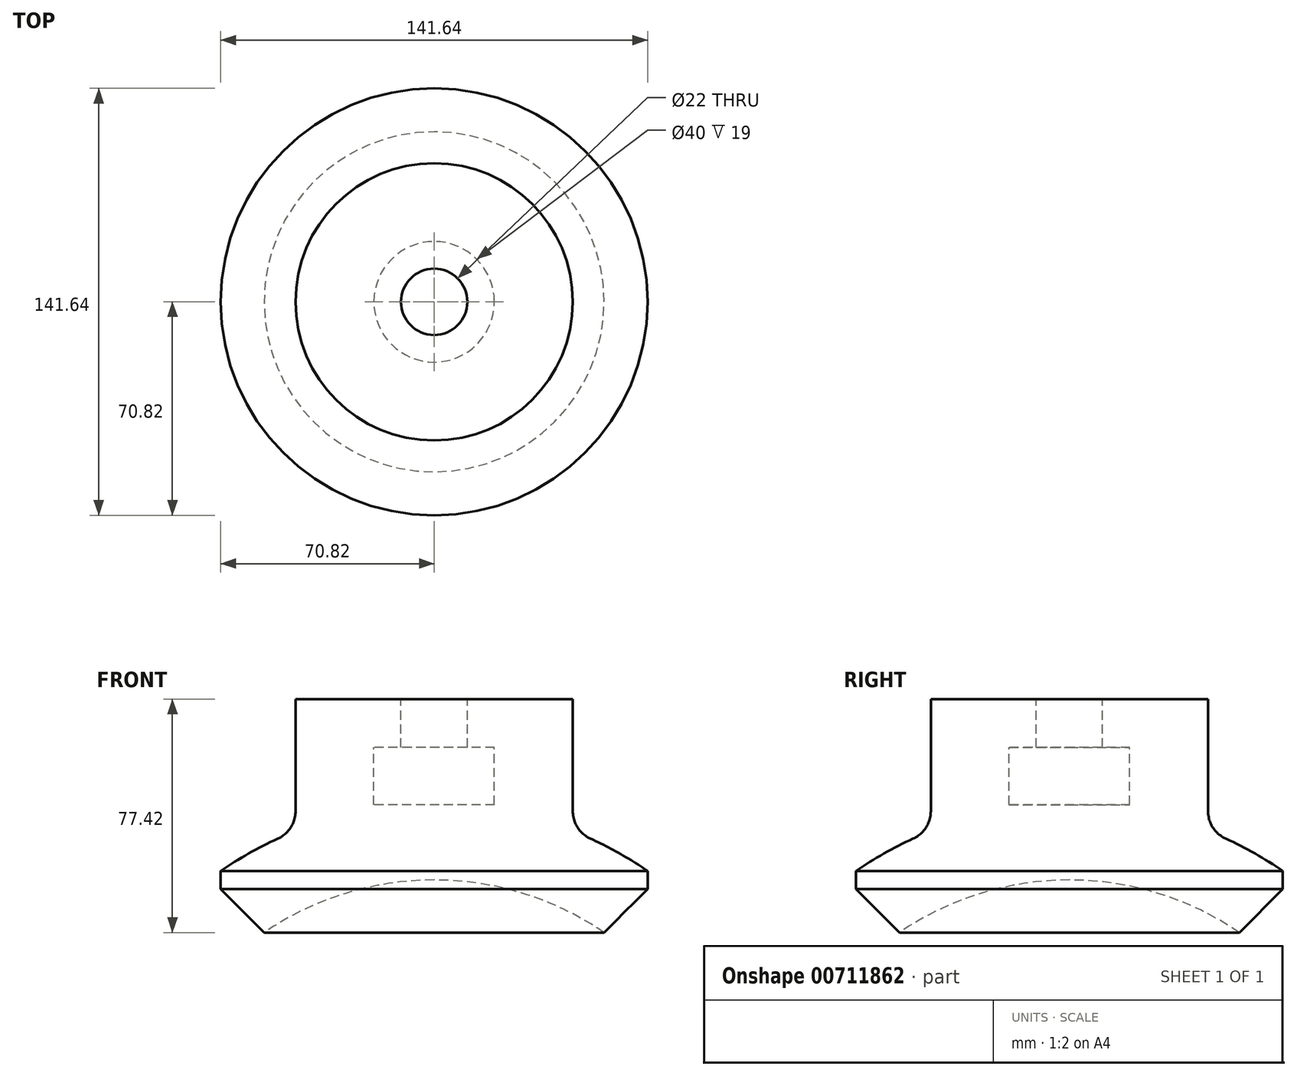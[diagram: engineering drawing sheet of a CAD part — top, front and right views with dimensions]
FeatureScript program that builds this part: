
annotation { "Feature Type Name" : "Feature", "Feature Type Description" : "" }
export const myFeature = defineFeature(function(context is Context, id is Id, definition is map)
    precondition{}
    {
        {
            var Q0;
            Q0=qCreatedBy(makeId("Front.planeOp"),FACE);
            var sketch = newSketch(context, id + "F0", { "sketchPlane" : qUnion([Q0])});
            skLineSegment(sketch, "E0", {"start": v(0, 35) * mm, "end": v(0, 0) * mm, "construction": true});
            skLineSegment(sketch, "E1", {"start": v(0, 35) * mm, "end": v(11, 35) * mm, "construction": true});
            skLineSegment(sketch, "E2", {"start": v(11, 35) * mm, "end": v(46, 35) * mm});
            skLineSegment(sketch, "E3", {"start": v(46, 35) * mm, "end": v(46, -2.16) * mm});
            skArc(sketch, "E4", {"start": v(70.82, -22) * mm, "mid": v(61.57, -16.22) * mm, "end": v(51.85, -11.26) * mm});
            skLineSegment(sketch, "E5", {"start": v(11, 35) * mm, "end": v(11, 19) * mm});
            skLineSegment(sketch, "E6", {"start": v(11, 19) * mm, "end": v(20, 19) * mm});
            skLineSegment(sketch, "E7", {"start": v(20, 19) * mm, "end": v(20, 0) * mm});
            skLineSegment(sketch, "E8", {"start": v(20, 0) * mm, "end": v(0, 0) * mm});
            skArc(sketch, "E9", {"start": v(46, -2.16) * mm, "mid": v(47.59, -7.57) * mm, "end": v(51.85, -11.26) * mm});
            skPoint(sketch, "E10.orphan", {"position": v(46, 0) * mm});
            skLineSegment(sketch, "E11", {"start": v(0, -125) * mm, "end": v(0, -125) * mm});
            skArc(sketch, "E12", {"start": v(56.4, -42.42) * mm, "mid": v(29.52, -29.45) * mm, "end": v(0, -25) * mm});
            skPoint(sketch, "E13.orphan", {"position": v(-117.64, 8.2) * mm});
            skPoint(sketch, "E14.orphan", {"position": v(117.64, 8.2) * mm});
            skLineSegment(sketch, "E15", {"start": v(70.82, -22) * mm, "end": v(70.82, -28) * mm});
            skLineSegment(sketch, "E16", {"start": v(70.82, -28) * mm, "end": v(56.4, -42.42) * mm});
            skPoint(sketch, "E17.orphan", {"position": v(62.5, -46.94) * mm});
            skLineSegment(sketch, "E18", {"start": v(0, 0) * mm, "end": v(0, -25) * mm});
            skPoint(sketch, "E19.orphan", {"position": v(-62.5, -46.94) * mm});
            skSolve(sketch);
        }
        {
            var Q0;
            Q0 = qSketchRegion(id + "F0", true);
            var Q1;
            Q1=sQuery(id+"F0.wireOp",EDGE,"E0");
            revolve(context, id + "F1", {"surfaceOperationType" : NewSurfaceOperationType.NEW, "entities" : qUnion([Q0]), "axis" : qUnion([Q1]), "revolveType" : RevolveType.FULL});
        }
    });
